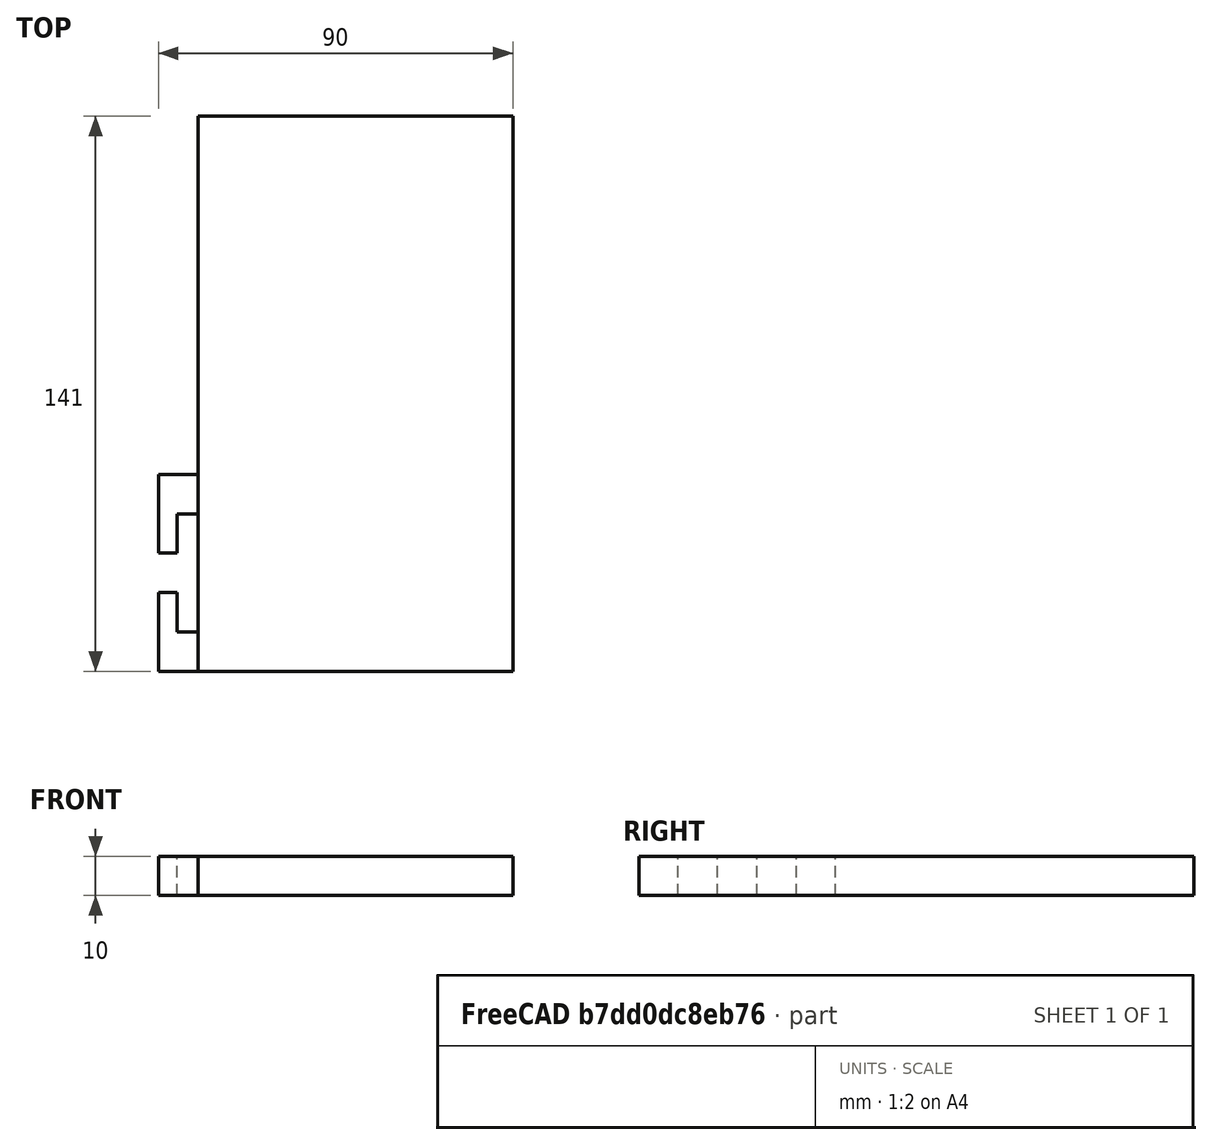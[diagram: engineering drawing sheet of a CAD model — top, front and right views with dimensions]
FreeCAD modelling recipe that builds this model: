
FCSTD DOCUMENT  (FreeCAD 0.21R33771 (Git))
Label: stand-tray-2
License: All rights reserved
LicenseURL: http://en.wikipedia.org/wiki/All_rights_reserved
objects: Part::Box×4, Part::Cut×2, App::DocumentObjectGroup×1
note: 6 computed .brp shape members not serialized (recipe doc carries the construction recipe); baked Part::Feature solids carry a one-line shape summary decoded from their .brp

FEATURE [Part::Box] Box  label="Cube"
  AttacherType = Attacher::AttachEngine3D
  Height = 10
  Length = 80
  Placement = pos=(-40,0,0) rot=(0,0,1;0rad)
  Width = 141
FEATURE [Part::Box] Box001  label="flansh"
  AttacherType = Attacher::AttachEngine3D
  Height = 10
  Length = 10
  Placement = pos=(-50,0,0) rot=(0,0,1;0rad)
  Width = 50
FEATURE [Part::Box] Box002  label="nut-1"
  AttacherType = Attacher::AttachEngine3D
  Height = 10
  Length = 5.25
  Placement = pos=(-45.25,10,0) rot=(0,0,1;0rad)
  Width = 30
FEATURE [Part::Box] Box003  label="nut-2"
  AttacherType = Attacher::AttachEngine3D
  Height = 10
  Length = 10
  Placement = pos=(-50,20,0) rot=(0,0,1;0rad)
  Width = 10
FEATURE [Part::Cut] Cut
  Base = -> Box001
  Tool = -> Box002
FEATURE [Part::Cut] Cut001
  Base = -> Cut
  Tool = -> Box003
FEATURE [App::DocumentObjectGroup] Group
  Group = -> [Cut001,Box]
